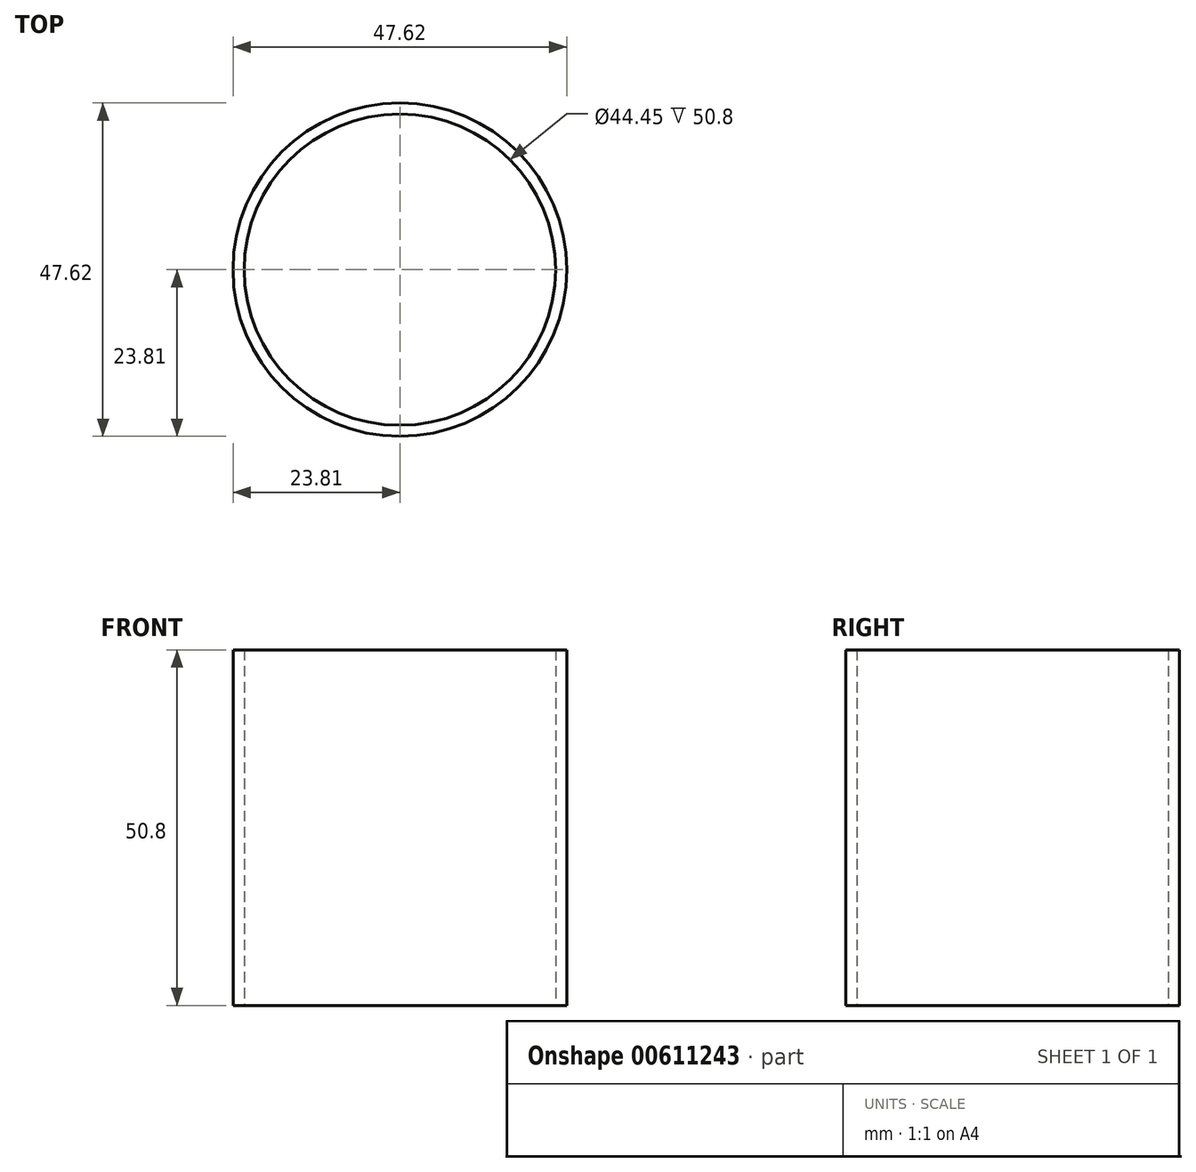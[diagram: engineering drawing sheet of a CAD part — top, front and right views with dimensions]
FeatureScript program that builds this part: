
annotation { "Feature Type Name" : "Feature", "Feature Type Description" : "" }
export const myFeature = defineFeature(function(context is Context, id is Id, definition is map)
    precondition{}
    {
        {
            var Q0;
            Q0=qCreatedBy(makeId("Top.planeOp"),FACE);
            var sketch = newSketch(context, id + "F0", { "sketchPlane" : qUnion([Q0])});
            skCircle(sketch, "E0", {"center": v(0, 0) * mm, "radius": 23.81 * mm});
            skCircle(sketch, "E1", {"center": v(0, 0) * mm, "radius": 22.23 * mm});
            skSolve(sketch);
        }
        {
            var Q0;
            Q0=makeQuery(id+"F0.imprint","IMPRINT",FACE,{"disambiguationData":[TD([[makeQuery(id+"F0.imprint","IMPRINT",EDGE,{"derivedFrom":sQuery(id+"F0.wireOp",EDGE,"E0")}),1.0]])]});
            extrude(context, id + "F1", {"entities" : qUnion([Q0]), "depth" : 50.8 * mm, "offsetDistance" : 25.4 * mm});
        }
    });
